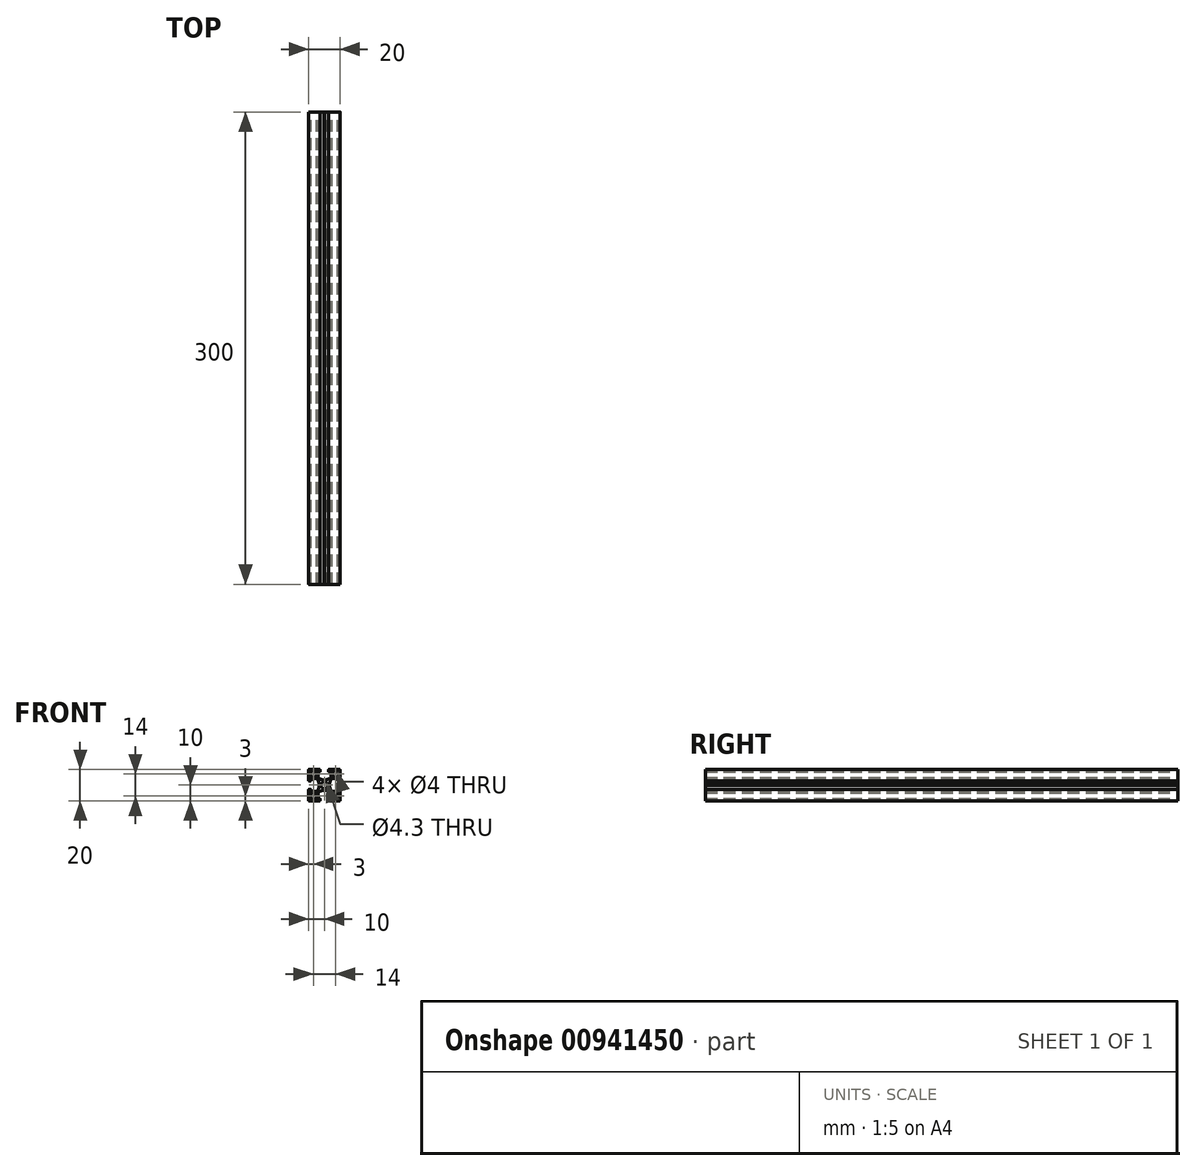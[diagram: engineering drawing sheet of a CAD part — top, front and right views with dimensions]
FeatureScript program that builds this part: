
annotation { "Feature Type Name" : "Feature", "Feature Type Description" : "" }
export const myFeature = defineFeature(function(context is Context, id is Id, definition is map)
    precondition{}
    {
        {
            var Q0;
            Q0=qCreatedBy(makeId("Front.planeOp"),FACE);
            var sketch = newSketch(context, id + "F0", { "sketchPlane" : qUnion([Q0])});
            skLineSegment(sketch, "E0", {"start": v(-11.2, 0) * mm, "end": v(11.2, 0) * mm});
            skCircle(sketch, "E1", {"center": v(0, 0) * mm, "radius": 2.15 * mm});
            skLineSegment(sketch, "E2", {"start": v(4.15, 4.94) * mm, "end": v(4.15, 8.2) * mm});
            skArc(sketch, "E3", {"start": v(4.15, 8.2) * mm, "mid": v(4.06, 8.41) * mm, "end": v(3.85, 8.5) * mm});
            skLineSegment(sketch, "E4", {"start": v(3.85, 8.5) * mm, "end": v(2.95, 8.5) * mm});
            skArc(sketch, "E5", {"start": v(2.95, 8.5) * mm, "mid": v(2.74, 8.59) * mm, "end": v(2.65, 8.8) * mm});
            skLineSegment(sketch, "E6", {"start": v(2.65, 8.8) * mm, "end": v(2.65, 9.7) * mm});
            skArc(sketch, "E7", {"start": v(2.65, 9.7) * mm, "mid": v(2.74, 9.91) * mm, "end": v(2.95, 10) * mm});
            skLineSegment(sketch, "E8", {"start": v(2.95, 10) * mm, "end": v(9.7, 10) * mm});
            skArc(sketch, "E9", {"start": v(9.7, 10) * mm, "mid": v(9.91, 9.91) * mm, "end": v(10, 9.7) * mm});
            skLineSegment(sketch, "E10", {"start": v(10, 9.7) * mm, "end": v(10, 2.95) * mm});
            skArc(sketch, "E11", {"start": v(10, 2.95) * mm, "mid": v(9.91, 2.74) * mm, "end": v(9.7, 2.65) * mm});
            skLineSegment(sketch, "E12", {"start": v(9.7, 2.65) * mm, "end": v(8.8, 2.65) * mm});
            skArc(sketch, "E13", {"start": v(8.8, 2.65) * mm, "mid": v(8.59, 2.74) * mm, "end": v(8.5, 2.95) * mm});
            skLineSegment(sketch, "E14", {"start": v(8.5, 2.95) * mm, "end": v(8.5, 3.85) * mm});
            skArc(sketch, "E15", {"start": v(8.5, 3.85) * mm, "mid": v(8.41, 4.06) * mm, "end": v(8.2, 4.15) * mm});
            skLineSegment(sketch, "E16", {"start": v(8.2, 4.15) * mm, "end": v(4.94, 4.15) * mm});
            skArc(sketch, "E17", {"start": v(4.94, 4.15) * mm, "mid": v(4.81, 4.12) * mm, "end": v(4.7, 4.04) * mm});
            skArc(sketch, "E18", {"start": v(4.7, 4.04) * mm, "mid": v(3.71, 2.28) * mm, "end": v(3.3, 0.3) * mm});
            skLineSegment(sketch, "E19", {"start": v(3.3, 0.3) * mm, "end": v(3, 0) * mm});
            skLineSegment(sketch, "E20", {"start": v(3, 0) * mm, "end": v(3.3, -0.3) * mm});
            skArc(sketch, "E21", {"start": v(3.3, -0.3) * mm, "mid": v(3.71, -2.28) * mm, "end": v(4.7, -4.04) * mm});
            skArc(sketch, "E22", {"start": v(4.7, -4.04) * mm, "mid": v(4.81, -4.12) * mm, "end": v(4.94, -4.15) * mm});
            skLineSegment(sketch, "E23", {"start": v(4.94, -4.15) * mm, "end": v(8.2, -4.15) * mm});
            skArc(sketch, "E24", {"start": v(8.2, -4.15) * mm, "mid": v(8.41, -4.06) * mm, "end": v(8.5, -3.85) * mm});
            skLineSegment(sketch, "E25", {"start": v(8.5, -3.85) * mm, "end": v(8.5, -2.95) * mm});
            skArc(sketch, "E26", {"start": v(8.5, -2.95) * mm, "mid": v(8.59, -2.74) * mm, "end": v(8.8, -2.65) * mm});
            skLineSegment(sketch, "E27", {"start": v(8.8, -2.65) * mm, "end": v(9.7, -2.65) * mm});
            skArc(sketch, "E28", {"start": v(9.7, -2.65) * mm, "mid": v(9.91, -2.74) * mm, "end": v(10, -2.95) * mm});
            skLineSegment(sketch, "E29", {"start": v(10, -2.95) * mm, "end": v(10, -9.7) * mm});
            skArc(sketch, "E30", {"start": v(10, -9.7) * mm, "mid": v(9.91, -9.91) * mm, "end": v(9.7, -10) * mm});
            skLineSegment(sketch, "E31", {"start": v(9.7, -10) * mm, "end": v(2.95, -10) * mm});
            skArc(sketch, "E32", {"start": v(2.95, -10) * mm, "mid": v(2.74, -9.91) * mm, "end": v(2.65, -9.7) * mm});
            skLineSegment(sketch, "E33", {"start": v(2.65, -9.7) * mm, "end": v(2.65, -8.8) * mm});
            skArc(sketch, "E34", {"start": v(2.65, -8.8) * mm, "mid": v(2.74, -8.59) * mm, "end": v(2.95, -8.5) * mm});
            skLineSegment(sketch, "E35", {"start": v(2.95, -8.5) * mm, "end": v(3.85, -8.5) * mm});
            skArc(sketch, "E36", {"start": v(3.85, -8.5) * mm, "mid": v(4.06, -8.41) * mm, "end": v(4.15, -8.2) * mm});
            skLineSegment(sketch, "E37", {"start": v(4.15, -8.2) * mm, "end": v(4.15, -4.94) * mm});
            skArc(sketch, "E38", {"start": v(4.15, -4.94) * mm, "mid": v(4.12, -4.81) * mm, "end": v(4.04, -4.7) * mm});
            skArc(sketch, "E39", {"start": v(4.04, -4.7) * mm, "mid": v(2.28, -3.71) * mm, "end": v(0.3, -3.3) * mm});
            skLineSegment(sketch, "E40", {"start": v(0.3, -3.3) * mm, "end": v(0, -3) * mm});
            skLineSegment(sketch, "E41", {"start": v(0, -3) * mm, "end": v(-0.3, -3.3) * mm});
            skArc(sketch, "E42", {"start": v(-0.3, -3.3) * mm, "mid": v(-2.28, -3.71) * mm, "end": v(-4.04, -4.7) * mm});
            skArc(sketch, "E43", {"start": v(-4.04, -4.7) * mm, "mid": v(-4.12, -4.81) * mm, "end": v(-4.15, -4.94) * mm});
            skLineSegment(sketch, "E44", {"start": v(-4.15, -4.94) * mm, "end": v(-4.15, -8.2) * mm});
            skArc(sketch, "E45", {"start": v(-4.15, -8.2) * mm, "mid": v(-4.06, -8.41) * mm, "end": v(-3.85, -8.5) * mm});
            skLineSegment(sketch, "E46", {"start": v(-3.85, -8.5) * mm, "end": v(-2.95, -8.5) * mm});
            skArc(sketch, "E47", {"start": v(-2.95, -8.5) * mm, "mid": v(-2.74, -8.59) * mm, "end": v(-2.65, -8.8) * mm});
            skLineSegment(sketch, "E48", {"start": v(-2.65, -8.8) * mm, "end": v(-2.65, -9.7) * mm});
            skArc(sketch, "E49", {"start": v(-2.65, -9.7) * mm, "mid": v(-2.74, -9.91) * mm, "end": v(-2.95, -10) * mm});
            skLineSegment(sketch, "E50", {"start": v(-2.95, -10) * mm, "end": v(-9.7, -10) * mm});
            skArc(sketch, "E51", {"start": v(-9.7, -10) * mm, "mid": v(-9.91, -9.91) * mm, "end": v(-10, -9.7) * mm});
            skLineSegment(sketch, "E52", {"start": v(-10, -9.7) * mm, "end": v(-10, -2.95) * mm});
            skArc(sketch, "E53", {"start": v(-10, -2.95) * mm, "mid": v(-9.91, -2.74) * mm, "end": v(-9.7, -2.65) * mm});
            skLineSegment(sketch, "E54", {"start": v(-9.7, -2.65) * mm, "end": v(-8.8, -2.65) * mm});
            skArc(sketch, "E55", {"start": v(-8.8, -2.65) * mm, "mid": v(-8.59, -2.74) * mm, "end": v(-8.5, -2.95) * mm});
            skLineSegment(sketch, "E56", {"start": v(-8.5, -2.95) * mm, "end": v(-8.5, -3.85) * mm});
            skArc(sketch, "E57", {"start": v(-8.5, -3.85) * mm, "mid": v(-8.41, -4.06) * mm, "end": v(-8.2, -4.15) * mm});
            skLineSegment(sketch, "E58", {"start": v(-8.2, -4.15) * mm, "end": v(-4.94, -4.15) * mm});
            skArc(sketch, "E59", {"start": v(-4.94, -4.15) * mm, "mid": v(-4.81, -4.12) * mm, "end": v(-4.7, -4.04) * mm});
            skArc(sketch, "E60", {"start": v(-4.7, -4.04) * mm, "mid": v(-3.71, -2.28) * mm, "end": v(-3.3, -0.3) * mm});
            skLineSegment(sketch, "E61", {"start": v(-3.3, -0.3) * mm, "end": v(-3, 0) * mm});
            skLineSegment(sketch, "E62", {"start": v(-3, 0) * mm, "end": v(-3.3, 0.3) * mm});
            skArc(sketch, "E63", {"start": v(-3.3, 0.3) * mm, "mid": v(-3.71, 2.28) * mm, "end": v(-4.7, 4.04) * mm});
            skArc(sketch, "E64", {"start": v(-4.7, 4.04) * mm, "mid": v(-4.81, 4.12) * mm, "end": v(-4.94, 4.15) * mm});
            skLineSegment(sketch, "E65", {"start": v(-4.94, 4.15) * mm, "end": v(-8.2, 4.15) * mm});
            skArc(sketch, "E66", {"start": v(-8.2, 4.15) * mm, "mid": v(-8.41, 4.06) * mm, "end": v(-8.5, 3.85) * mm});
            skLineSegment(sketch, "E67", {"start": v(-8.5, 3.85) * mm, "end": v(-8.5, 2.95) * mm});
            skArc(sketch, "E68", {"start": v(-8.5, 2.95) * mm, "mid": v(-8.59, 2.74) * mm, "end": v(-8.8, 2.65) * mm});
            skLineSegment(sketch, "E69", {"start": v(-8.8, 2.65) * mm, "end": v(-9.7, 2.65) * mm});
            skArc(sketch, "E70", {"start": v(-9.7, 2.65) * mm, "mid": v(-9.91, 2.74) * mm, "end": v(-10, 2.95) * mm});
            skLineSegment(sketch, "E71", {"start": v(-10, 2.95) * mm, "end": v(-10, 9.7) * mm});
            skArc(sketch, "E72", {"start": v(-10, 9.7) * mm, "mid": v(-9.91, 9.91) * mm, "end": v(-9.7, 10) * mm});
            skLineSegment(sketch, "E73", {"start": v(-9.7, 10) * mm, "end": v(-2.95, 10) * mm});
            skArc(sketch, "E74", {"start": v(-2.95, 10) * mm, "mid": v(-2.74, 9.91) * mm, "end": v(-2.65, 9.7) * mm});
            skLineSegment(sketch, "E75", {"start": v(-2.65, 9.7) * mm, "end": v(-2.65, 8.8) * mm});
            skArc(sketch, "E76", {"start": v(-2.65, 8.8) * mm, "mid": v(-2.74, 8.59) * mm, "end": v(-2.95, 8.5) * mm});
            skLineSegment(sketch, "E77", {"start": v(-2.95, 8.5) * mm, "end": v(-3.85, 8.5) * mm});
            skArc(sketch, "E78", {"start": v(-3.85, 8.5) * mm, "mid": v(-4.06, 8.41) * mm, "end": v(-4.15, 8.2) * mm});
            skLineSegment(sketch, "E79", {"start": v(-4.15, 8.2) * mm, "end": v(-4.15, 4.94) * mm});
            skArc(sketch, "E80", {"start": v(-4.15, 4.94) * mm, "mid": v(-4.12, 4.81) * mm, "end": v(-4.04, 4.7) * mm});
            skArc(sketch, "E81", {"start": v(-4.04, 4.7) * mm, "mid": v(-2.28, 3.71) * mm, "end": v(-0.3, 3.3) * mm});
            skLineSegment(sketch, "E82", {"start": v(-0.3, 3.3) * mm, "end": v(0, 3) * mm});
            skLineSegment(sketch, "E83", {"start": v(0, 3) * mm, "end": v(0.3, 3.3) * mm});
            skArc(sketch, "E84", {"start": v(0.3, 3.3) * mm, "mid": v(2.28, 3.71) * mm, "end": v(4.04, 4.7) * mm});
            skArc(sketch, "E85", {"start": v(4.04, 4.7) * mm, "mid": v(4.12, 4.81) * mm, "end": v(4.15, 4.94) * mm});
            skLineSegment(sketch, "E86", {"start": v(-9.5, 7) * mm, "end": v(-4.5, 7) * mm});
            skLineSegment(sketch, "E87", {"start": v(-7, 9.5) * mm, "end": v(-7, 4.5) * mm});
            skCircle(sketch, "E88", {"center": v(-7, 7) * mm, "radius": 2 * mm});
            skLineSegment(sketch, "E89", {"start": v(-9.5, -7) * mm, "end": v(-4.5, -7) * mm});
            skLineSegment(sketch, "E90", {"start": v(-7, -9.5) * mm, "end": v(-7, -4.5) * mm});
            skCircle(sketch, "E91", {"center": v(-7, -7) * mm, "radius": 2 * mm});
            skLineSegment(sketch, "E92", {"start": v(0, 11.2) * mm, "end": v(0, -11.2) * mm});
            skLineSegment(sketch, "E93", {"start": v(9.5, 7) * mm, "end": v(4.5, 7) * mm});
            skLineSegment(sketch, "E94", {"start": v(7, 9.5) * mm, "end": v(7, 4.5) * mm});
            skCircle(sketch, "E95", {"center": v(7, 7) * mm, "radius": 2 * mm});
            skCircle(sketch, "E96", {"center": v(7, -7) * mm, "radius": 2 * mm});
            skLineSegment(sketch, "E97", {"start": v(7, -9.5) * mm, "end": v(7, -4.5) * mm});
            skLineSegment(sketch, "E98", {"start": v(9.5, -7) * mm, "end": v(4.5, -7) * mm});
            skSolve(sketch);
        }
        {
            var Q0;
            Q0=makeQuery(id+"F0.imprint","IMPRINT",FACE,{"disambiguationData":[TD([[makeQuery(id+"F0.imprint","IMPRINT",EDGE,{"derivedFrom":sQuery(id+"F0.wireOp",EDGE,"E2")}),-1.0]])]});
            var Q1;
            {var subQ10=sQuery(id+"F0.wireOp",EDGE,"E20");Q1=makeQuery(id+"F0.imprint","IMPRINT",FACE,{"disambiguationData":[TD([[makeQuery(id+"F0.imprint","IMPRINT",EDGE,{"derivedFrom":subQ10}),-1.0]])]});}
            var Q2;
            {var subQ1=sQuery(id+"F0.wireOp",EDGE,"E41");Q2=makeQuery(id+"F0.imprint","IMPRINT",FACE,{"disambiguationData":[TD([[makeQuery(id+"F0.imprint","IMPRINT",EDGE,{"derivedFrom":subQ1}),-1.0]])]});}
            var Q3;
            {var subQ0=sQuery(id+"F0.wireOp",EDGE,"E62");Q3=makeQuery(id+"F0.imprint","IMPRINT",FACE,{"disambiguationData":[TD([[makeQuery(id+"F0.imprint","IMPRINT",EDGE,{"derivedFrom":subQ0}),-1.0]])]});}
            extrude(context, id + "F1", {"entities" : qUnion([Q0, Q1, Q2, Q3]), "depth" : 300 * mm, "offsetDistance" : 25 * mm});
        }
    });
